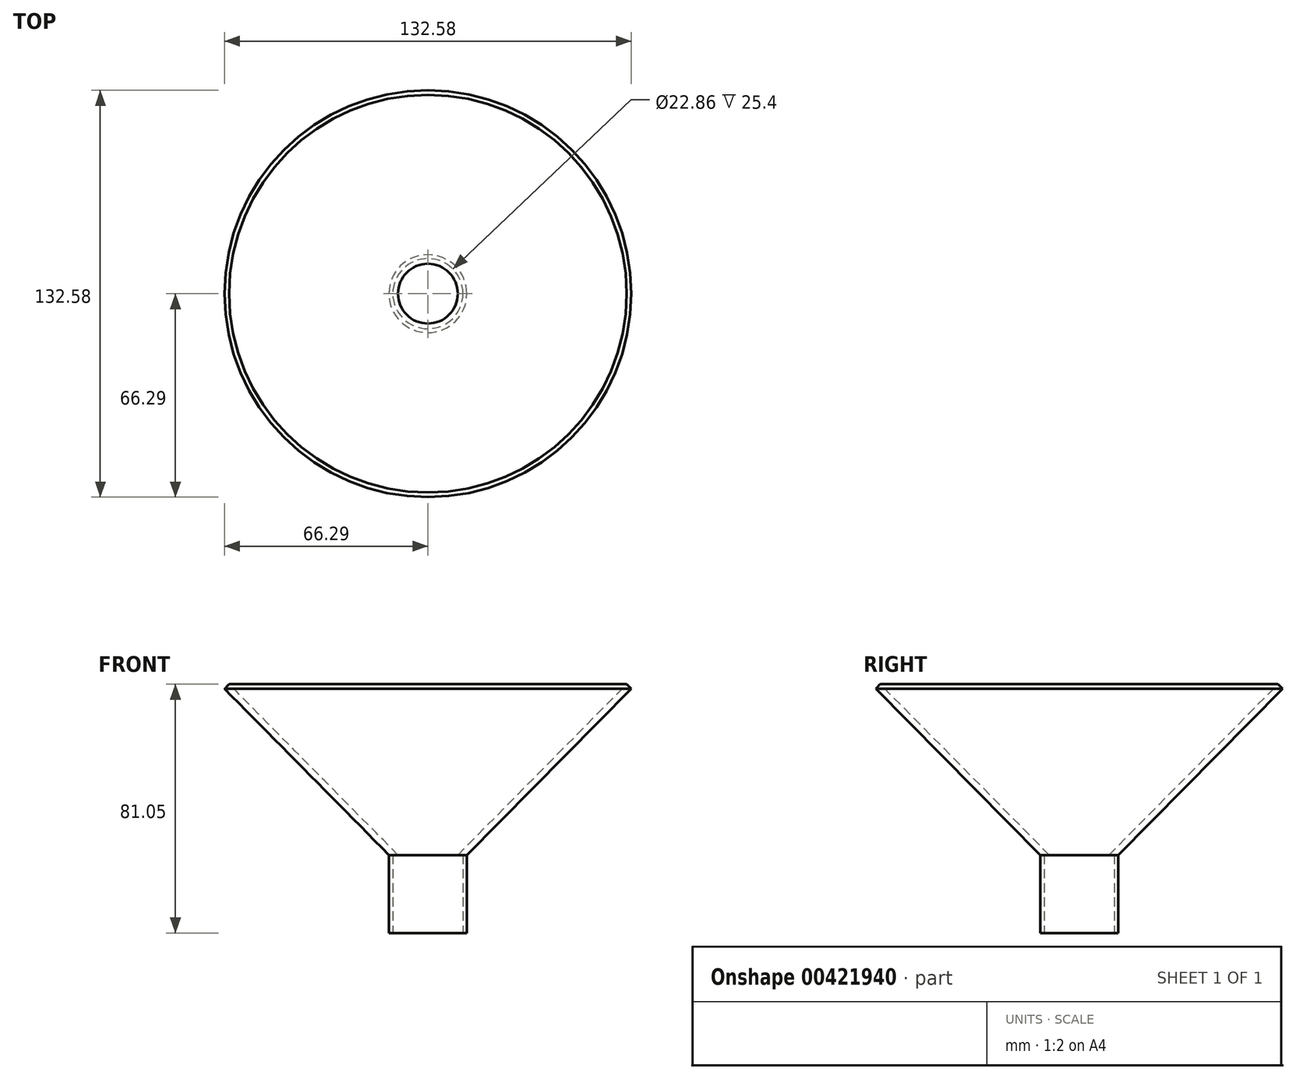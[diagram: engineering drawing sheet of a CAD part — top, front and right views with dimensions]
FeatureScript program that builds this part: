
annotation { "Feature Type Name" : "Feature", "Feature Type Description" : "" }
export const myFeature = defineFeature(function(context is Context, id is Id, definition is map)
    precondition{}
    {
        {
            var Q0;
            Q0=qCreatedBy(makeId("Front.planeOp"),FACE);
            var sketch = newSketch(context, id + "F0", { "sketchPlane" : qUnion([Q0])});
            skLineSegment(sketch, "E0", {"start": v(12.7, -9.36) * mm, "end": v(12.7, 16.04) * mm});
            skLineSegment(sketch, "E1", {"start": v(12.7, 16.04) * mm, "end": v(66.3, 70.21) * mm});
            skLineSegment(sketch, "E2", {"start": v(66.3, 70.21) * mm, "end": v(61.43, 75.02) * mm});
            skLineSegment(sketch, "E3", {"start": v(12.7, -9.36) * mm, "end": v(0, -9.36) * mm});
            skLineSegment(sketch, "E4", {"start": v(0, -9.36) * mm, "end": v(0, 16.04) * mm});
            skLineSegment(sketch, "E5", {"start": v(0, 16.04) * mm, "end": v(9.74, 16.04) * mm});
            skLineSegment(sketch, "E6", {"start": v(9.74, 16.04) * mm, "end": v(63.33, 70.21) * mm});
            skLineSegment(sketch, "E7", {"start": v(63.33, 70.21) * mm, "end": v(64.8, 71.7) * mm});
            skSolve(sketch);
        }
        {
            var Q0;
            Q0=makeQuery(id+"F0.imprint","IMPRINT",FACE,{"disambiguationData":[TD([[makeQuery(id+"F0.imprint","IMPRINT",EDGE,{"derivedFrom":sQuery(id+"F0.wireOp",EDGE,"E0")}),1.0]])]});
            var Q1;
            Q1=sQuery(id+"F0.wireOp",EDGE,"E4");
            revolve(context, id + "F1", {"entities" : qUnion([Q0]), "axis" : qUnion([Q1]), "revolveType" : RevolveType.FULL});
        }
        {
            var Q0;
            Q0=makeQuery(id+"F1.opRevolve","SWEPT_FACE",FACE,{"disambiguationData":[OSD([sQuery(id+"F0.wireOp",EDGE,"E3")])]});
            extrude(context, id + "F2", {"entities" : qUnion([Q0]), "operationType" : NewBodyOperationType.REMOVE, "depth" : 25.4 * mm});
        }
        {
            var Q0;
            Q0=makeQuery(id+"F1.opRevolve","SWEPT_FACE",FACE,{"disambiguationData":[OSD([sQuery(id+"F0.wireOp",EDGE,"E3")])]});
            var sketch = newSketch(context, id + "F3", { "sketchPlane" : qUnion([Q0])});
            skCircle(sketch, "E8", {"center": v(0, 0) * mm, "radius": 11.43 * mm});
            skSolve(sketch);
        }
        {
            var Q0;
            Q0=makeQuery(id+"F3.imprint","IMPRINT",FACE,{"disambiguationData":[TD([[makeQuery(id+"F3.imprint","IMPRINT",EDGE,{"derivedFrom":sQuery(id+"F3.wireOp",EDGE,"E8")}),1.0]])]});
            extrude(context, id + "F4", {"entities" : qUnion([Q0]), "operationType" : NewBodyOperationType.REMOVE, "oppositeDirection" : true, "depth" : 25.4 * mm});
        }
    });
